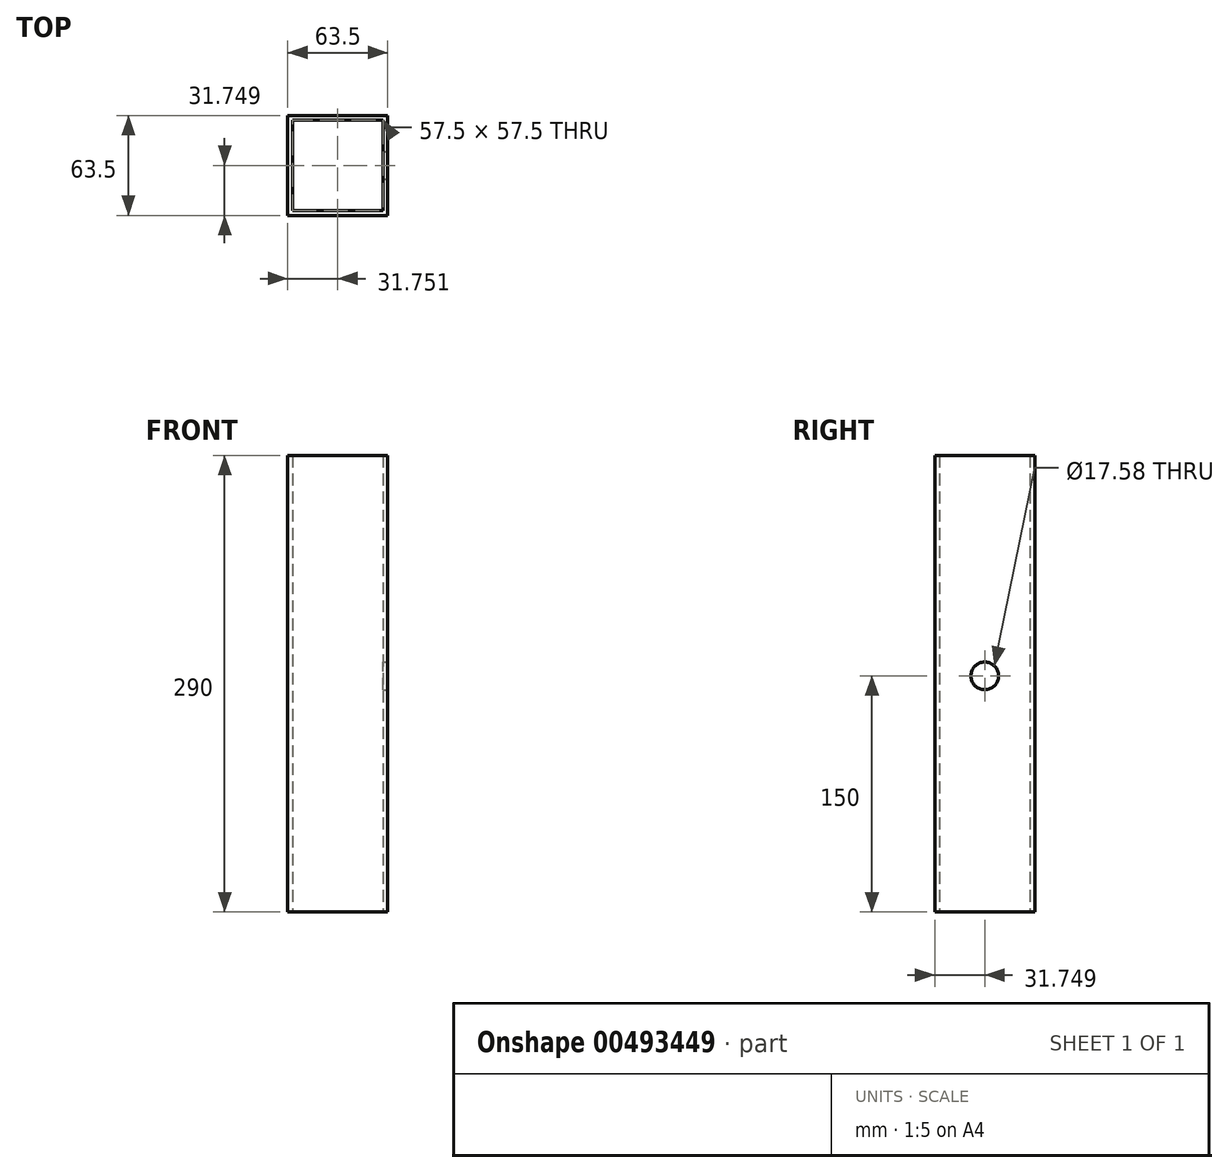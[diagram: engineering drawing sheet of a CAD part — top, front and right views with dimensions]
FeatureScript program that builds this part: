
annotation { "Feature Type Name" : "Feature", "Feature Type Description" : "" }
export const myFeature = defineFeature(function(context is Context, id is Id, definition is map)
    precondition{}
    {
        {
            var Q0;
            Q0=qCreatedBy(makeId("Top.planeOp"),FACE);
            var sketch = newSketch(context, id + "F0", { "sketchPlane" : qUnion([Q0])});
            skLineSegment(sketch, "E0.bottom", {"start": v(-26.72, 32.42) * mm, "end": v(30.78, 32.42) * mm});
            skLineSegment(sketch, "E0.top", {"start": v(-26.72, -25.08) * mm, "end": v(30.78, -25.08) * mm});
            skLineSegment(sketch, "E0.left", {"start": v(-26.72, 32.42) * mm, "end": v(-26.72, -25.08) * mm});
            skLineSegment(sketch, "E0.right", {"start": v(30.78, 32.42) * mm, "end": v(30.78, -25.08) * mm});
            skLineSegment(sketch, "E1.bottom", {"start": v(-29.72, 35.42) * mm, "end": v(33.78, 35.42) * mm});
            skLineSegment(sketch, "E1.top", {"start": v(-29.72, -28.08) * mm, "end": v(33.78, -28.08) * mm});
            skLineSegment(sketch, "E1.left", {"start": v(-29.72, 35.42) * mm, "end": v(-29.72, -28.08) * mm});
            skLineSegment(sketch, "E1.right", {"start": v(33.78, 35.42) * mm, "end": v(33.78, -28.08) * mm});
            skSolve(sketch);
        }
        {
            var Q0;
            Q0=qSketchRegion(id+"F0",true);
            extrude(context, id + "F1", {"entities" : qUnion([Q0]), "depth" : 290 * mm});
        }
        {
            var Q0;
            Q0=makeQuery(id+"F1.opExtrude","SWEPT_FACE",FACE,{"disambiguationData":[OSD([sQuery(id+"F0.wireOp",EDGE,"E1.right")])]});
            var sketch = newSketch(context, id + "F2", { "sketchPlane" : qUnion([Q0])});
            skCircle(sketch, "E2", {"center": v(3.67, 150) * mm, "radius": 8.8 * mm});
            skSolve(sketch);
        }
        {
            var Q0;
            Q0 = qSketchRegion(id + "F2", true);
            extrude(context, id + "F3", {"entities" : qUnion([Q0]), "operationType" : NewBodyOperationType.REMOVE, "oppositeDirection" : true, "depth" : 25 * mm});
        }
    });
